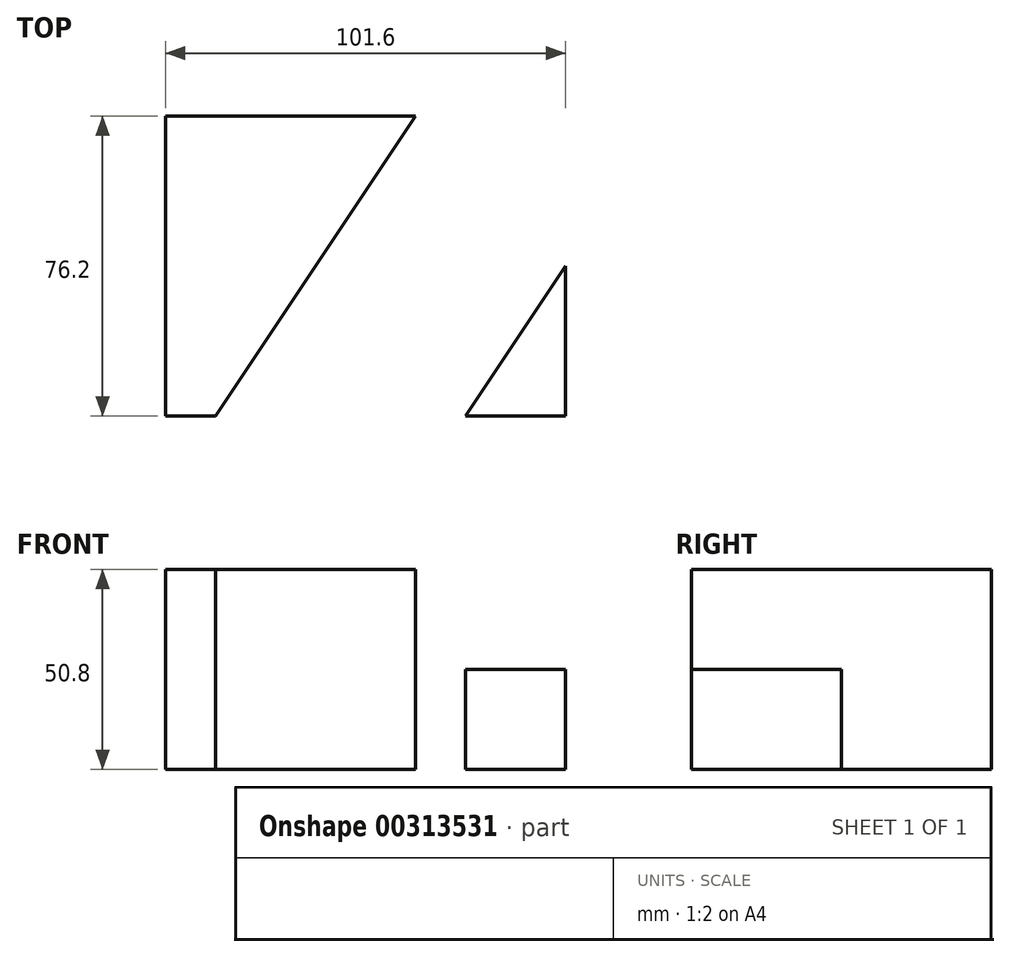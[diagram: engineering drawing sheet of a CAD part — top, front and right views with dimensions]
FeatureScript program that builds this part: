
annotation { "Feature Type Name" : "Feature", "Feature Type Description" : "" }
export const myFeature = defineFeature(function(context is Context, id is Id, definition is map)
    precondition{}
    {
        {
            var Q0;
            Q0=qCreatedBy(makeId("Top.planeOp"),FACE);
            var sketch = newSketch(context, id + "F0", { "sketchPlane" : qUnion([Q0])});
            skLineSegment(sketch, "E0", {"start": v(-64.45, 37.64) * mm, "end": v(-64.45, -38.56) * mm});
            skLineSegment(sketch, "E1", {"start": v(-64.45, -38.56) * mm, "end": v(37.15, -38.56) * mm});
            skLineSegment(sketch, "E2", {"start": v(37.15, -38.56) * mm, "end": v(37.15, 37.64) * mm});
            skLineSegment(sketch, "E3", {"start": v(37.15, 37.64) * mm, "end": v(-64.45, 37.64) * mm});
            skLineSegment(sketch, "E4", {"start": v(-64.45, -38.56) * mm, "end": v(-51.75, -38.56) * mm});
            skLineSegment(sketch, "E5", {"start": v(-51.75, -38.56) * mm, "end": v(-0.95, 37.64) * mm});
            skLineSegment(sketch, "E6", {"start": v(-0.95, 37.64) * mm, "end": v(-64.45, 37.64) * mm});
            skLineSegment(sketch, "E7", {"start": v(37.15, -38.56) * mm, "end": v(11.75, -38.56) * mm});
            skLineSegment(sketch, "E8", {"start": v(11.75, -38.56) * mm, "end": v(37.15, -0.46) * mm});
            skLineSegment(sketch, "E9", {"start": v(37.15, -0.46) * mm, "end": v(37.15, -38.56) * mm});
            skSolve(sketch);
        }
        {
            var Q0;
            Q0=makeQuery(id+"F0.imprint","IMPRINT",FACE,{"disambiguationData":[TD([[makeQuery(id+"F0.imprint","IMPRINT",EDGE,{"derivedFrom":sQuery(id+"F0.wireOp",EDGE,"E0")}),1.0]])]});
            var Q1;
            Q1=makeQuery(id+"F0.imprint","IMPRINT",FACE,{"disambiguationData":[TD([[makeQuery(id+"F0.imprint","IMPRINT",EDGE,{"derivedFrom":sQuery(id+"F0.wireOp",EDGE,"E7")}),-1.0]])]});
            var Q2;
            Q2=makeQuery(id+"F0.imprint","IMPRINT",FACE,{"disambiguationData":[TD([[makeQuery(id+"F0.imprint","IMPRINT",EDGE,{"derivedFrom":sQuery(id+"F0.wireOp",EDGE,"E1")}),1.0]])]});
            extrude(context, id + "F1", {"entities" : qUnion([Q0, Q1, Q2]), "oppositeDirection" : true, "depth" : 25.4 * mm});
        }
        {
            var Q0;
            Q0=makeQuery(id+"F0.imprint","IMPRINT",FACE,{"disambiguationData":[TD([[makeQuery(id+"F0.imprint","IMPRINT",EDGE,{"derivedFrom":sQuery(id+"F0.wireOp",EDGE,"E7")}),-1.0]])]});
            var Q1;
            Q1=makeQuery(id+"F0.imprint","IMPRINT",FACE,{"disambiguationData":[TD([[makeQuery(id+"F0.imprint","IMPRINT",EDGE,{"derivedFrom":sQuery(id+"F0.wireOp",EDGE,"E0")}),1.0]])]});
            extrude(context, id + "F2", {"entities" : qUnion([Q0, Q1]), "operationType" : NewBodyOperationType.ADD, "depth" : 25.4 * mm});
        }
    });
